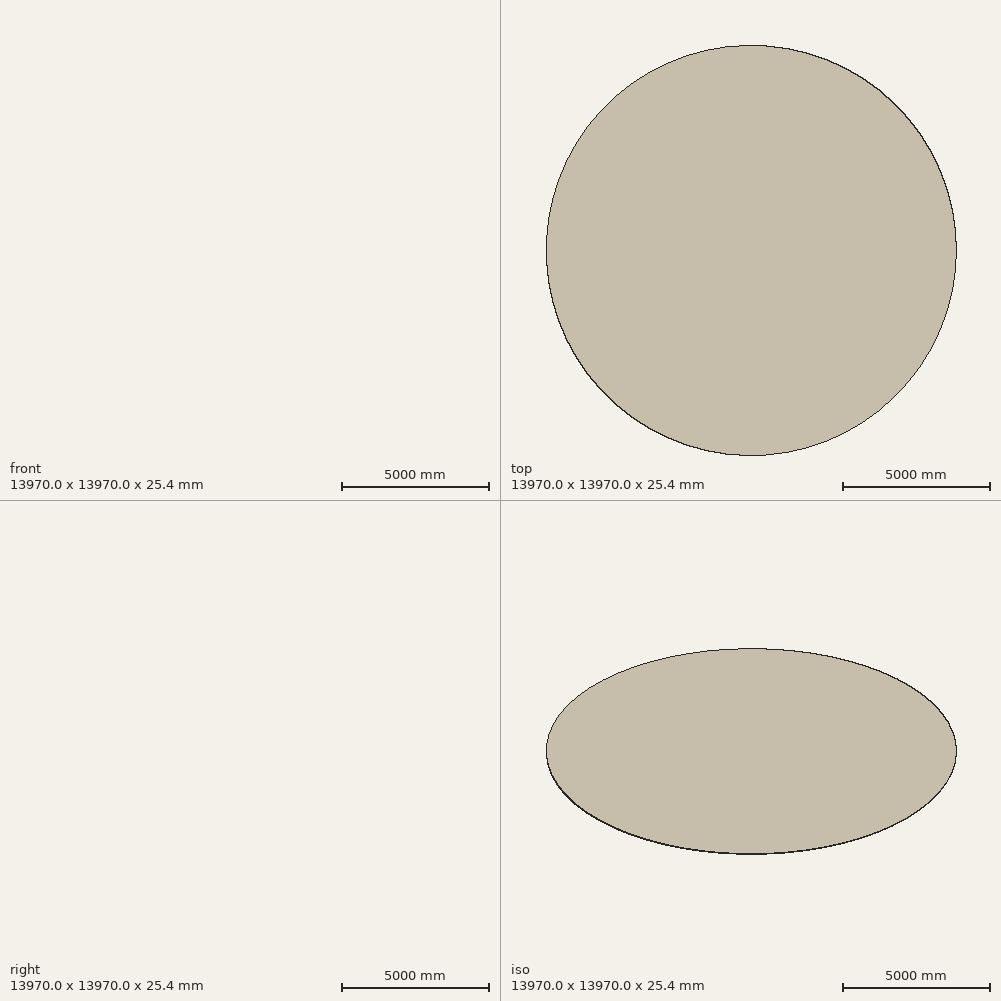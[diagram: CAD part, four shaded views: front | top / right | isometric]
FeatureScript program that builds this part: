
annotation { "Feature Type Name" : "Feature", "Feature Type Description" : "" }
export const myFeature = defineFeature(function(context is Context, id is Id, definition is map)
    precondition{}
    {
        {
            var Q0;
            Q0=qCreatedBy(makeId("Top.planeOp"),FACE);
            var sketch = newSketch(context, id + "F0", { "sketchPlane" : qUnion([Q0])});
            skPoint(sketch, "E0.center.orphan", {"position": v(43.03, 0) * mm});
            skPoint(sketch, "E1.center.orphan", {"position": v(32.95, 0) * mm});
            skCircle(sketch, "E2", {"center": v(-9.93, 18.56) * mm, "radius": 6.99 * mm});
            skCircle(sketch, "E3", {"center": v(10.22, 18.56) * mm, "radius": 6.99 * mm});
            skCircle(sketch, "E4", {"center": v(-9.93, -18.28) * mm, "radius": 6.99 * mm});
            skCircle(sketch, "E5", {"center": v(9.93, -18.28) * mm, "radius": 6985 * mm});
            skCircle(sketch, "E6", {"center": v(9.93, -18.28) * mm, "radius": 6.99 * mm});
            skSolve(sketch);
        }
        {
            var Q0;
            Q0 = qSketchRegion(id + "F0", true);
            extrude(context, id + "F1", {"entities" : qUnion([Q0]), "depth" : 25.4 * mm, "offsetDistance" : 25.4 * mm});
        }
    });
